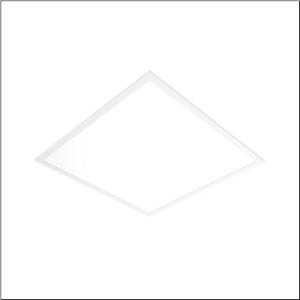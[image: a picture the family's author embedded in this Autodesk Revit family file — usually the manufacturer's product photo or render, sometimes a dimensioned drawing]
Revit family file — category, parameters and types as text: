
# Revit family: apollon_r__41_51mh12l72443_9cb4
name_source: partatom
category: Lighting Fixtures
units: mm (PartAtom-declared; Revit-internal decimal feet)

## family parameters
Cut with Voids When Loaded = No
Host = Face
Light Source = No
Part Type = Normal
Room Calculation Point = No
Round Connector Dimension = Use Diameter
Shared = No

## types (1)
- Apollon® 41 (1 x LED, 2800 lm, 21.5 W, 4000K)
    Apparent Load = 22 VA
    CIE Flux Codes = 61 87 97 100 100
    Color Rendering = 80
    Color Temperature = 4000K
    Default Elevation = 1800 mm
    Description = Apollon® 41, office luminaire, primary optical cover: prismatic diffuser, of PS, light emission: direct distribution, primary light characteristic: symmetric, installation type: lay-in mounting, LED, rated luminous flux: 2.800lm, luminous efficacy: 130lm/W, light colour: 840, colour temperature: 4000K, with terminal, 3-pole, mains connection: 220..240V, AC, 50/60Hz, rated input power: 21.5W, housing, of aluminium section, traffic white (RAL 9016), module: M600, length: 600mm, width: 600mm, height: 28mm, housing upper side, of sheet steel, protection rating (complete): IP20, protection rating (lamp compartment, on room side): IP40, insulation class (complete): insulation class II (safety insulation), certification: CE, ENEC, permissible operating ambient temperature: -25..+40°C, packaging unit: 1 piece
    Height = 0 mm  [stored 0 ft]
    Lamp = 1 x LED
    Lamp Light Flux = 2800 lm
    Lamp Power = 21.5 W
    Lamp count = 1
    Length = 600 mm
    Luminous efficacy = 130 lm/W
    Manufacturer = Siteco
    ModVariant = No
    Model = 51MH12L72443
    Mounting Place = Ceiling
    Mounting Type = Recessed
    Number of Poles = 1
    OnlyDefault = Yes
    Power Factor = 1
    Product Name = Apollon® 41
    Product group = office luminaire | ceiling recessed
    ProductGroupID = 401
    Protection Class = Protection class II
    Protection Degree = IP 20
    RLX_Detail_Level = 1
    RLX_Emergency_Light_Flux = 0 lm
    RLX_Emergency_Type = 0
    RLX_Emergency_Type_DB = No
    RlxData = <blob elided: 12201 chars, md5=1ec3f395>
    Socket = socket
    Standby Power = 0 W
    System Light Flux = 2800 lm
    System Power = 22 W
    Type Comments = Product without accessories
    Type Image = l_1291024.jpg
    URL = http://relux.com
    VarID = ---
    Voltage = 0 V
    Weight = 0.00 kg
    Width = 600 mm

note: [stored X ft] marks values corroborated as IEEE doubles in the binary element streams (Revit-internal decimal feet)

## geometry (parser evidence)
native form markers: Sweep x11
no freeform markers — native parametric forms only
